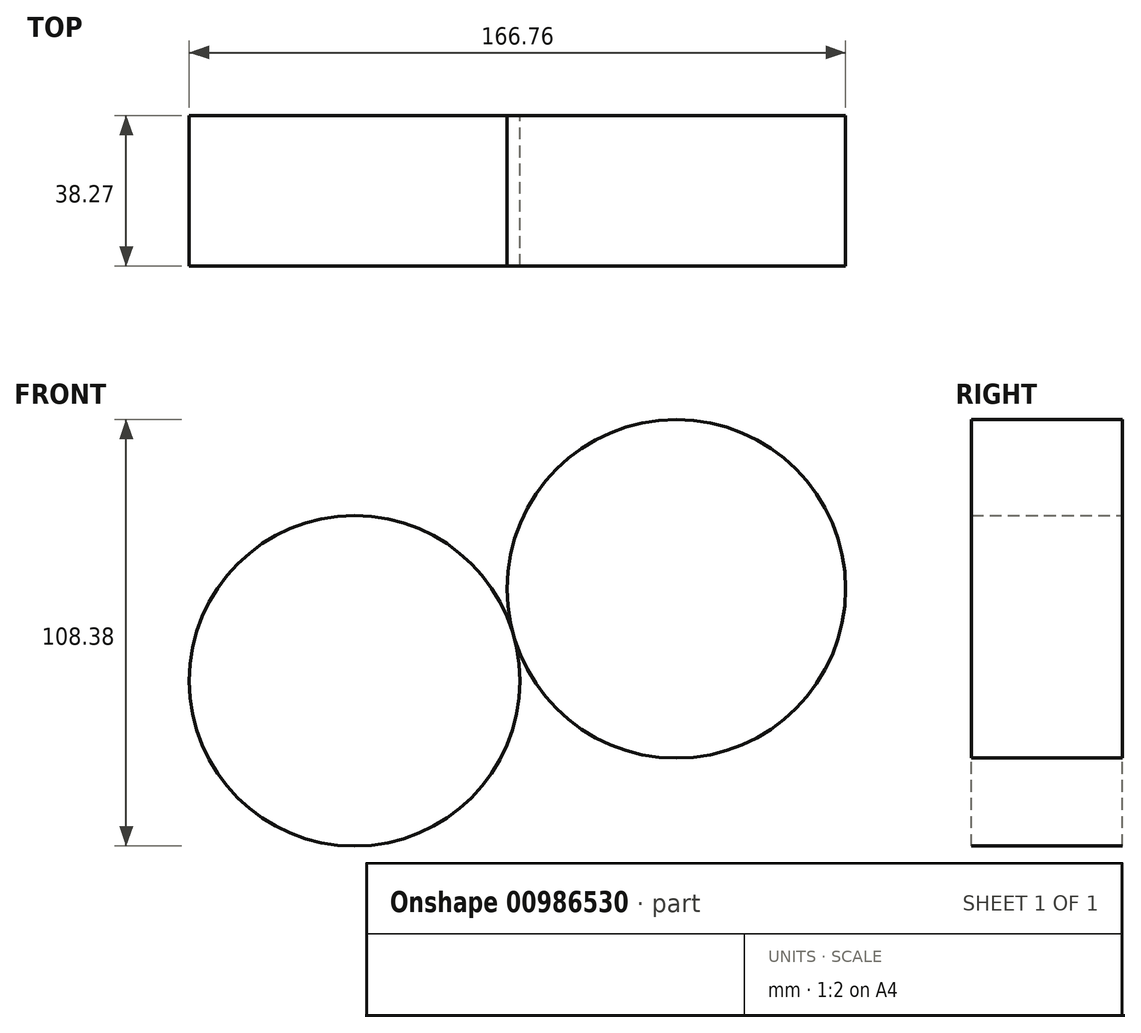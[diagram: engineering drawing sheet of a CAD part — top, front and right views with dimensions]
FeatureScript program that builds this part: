
annotation { "Feature Type Name" : "Feature", "Feature Type Description" : "" }
export const myFeature = defineFeature(function(context is Context, id is Id, definition is map)
    precondition{}
    {
        {
            var Q0;
            Q0=qCreatedBy(makeId("Front.planeOp"),FACE);
            var sketch = newSketch(context, id + "F0", { "sketchPlane" : qUnion([Q0])});
            skCircle(sketch, "E0", {"center": v(0, 0) * mm, "radius": 42 * mm});
            skCircle(sketch, "E1", {"center": v(81.74, 23.37) * mm, "radius": 43.02 * mm});
            skSolve(sketch);
        }
        {
            var Q0;
            Q0 = qSketchRegion(id + "F0", true);
            extrude(context, id + "F1", {"entities" : qUnion([Q0]), "depth" : 38.27 * mm, "offsetDistance" : 25 * mm});
        }
    });
